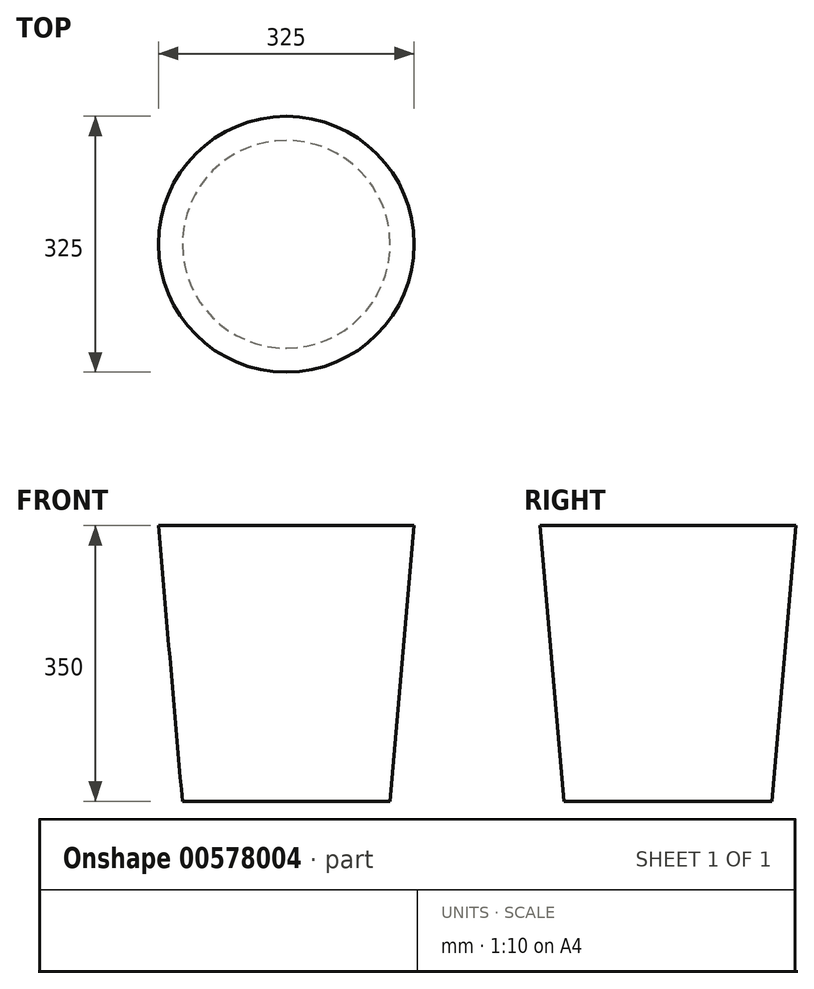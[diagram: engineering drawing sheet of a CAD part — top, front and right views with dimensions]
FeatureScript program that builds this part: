
annotation { "Feature Type Name" : "Feature", "Feature Type Description" : "" }
export const myFeature = defineFeature(function(context is Context, id is Id, definition is map)
    precondition{}
    {
        {
            var Q0;
            Q0=qCreatedBy(makeId("Front.planeOp"),FACE);
            var sketch = newSketch(context, id + "F0", { "sketchPlane" : qUnion([Q0])});
            skLineSegment(sketch, "E0", {"start": v(0, 0) * mm, "end": v(0, 101.35) * mm, "construction": true});
            skLineSegment(sketch, "E1", {"start": v(0, 0) * mm, "end": v(132, 0) * mm});
            skLineSegment(sketch, "E2", {"start": v(132, 0) * mm, "end": v(162.5, 350) * mm});
            skLineSegment(sketch, "E3", {"start": v(162.5, 350) * mm, "end": v(0, 350) * mm});
            skLineSegment(sketch, "E4", {"start": v(0, 350) * mm, "end": v(0, 0) * mm});
            skSolve(sketch);
        }
        {
            var Q0;
            Q0=makeQuery(id+"F0.imprint","IMPRINT",FACE,{"disambiguationData":[TD([[makeQuery(id+"F0.imprint","IMPRINT",EDGE,{"derivedFrom":sQuery(id+"F0.wireOp",EDGE,"E1")}),1.0]])]});
            var Q1;
            Q1=sQuery(id+"F0.wireOp",EDGE,"E0");
            revolve(context, id + "F1", {"entities" : qUnion([Q0]), "axis" : qUnion([Q1]), "revolveType" : RevolveType.FULL});
        }
    });
